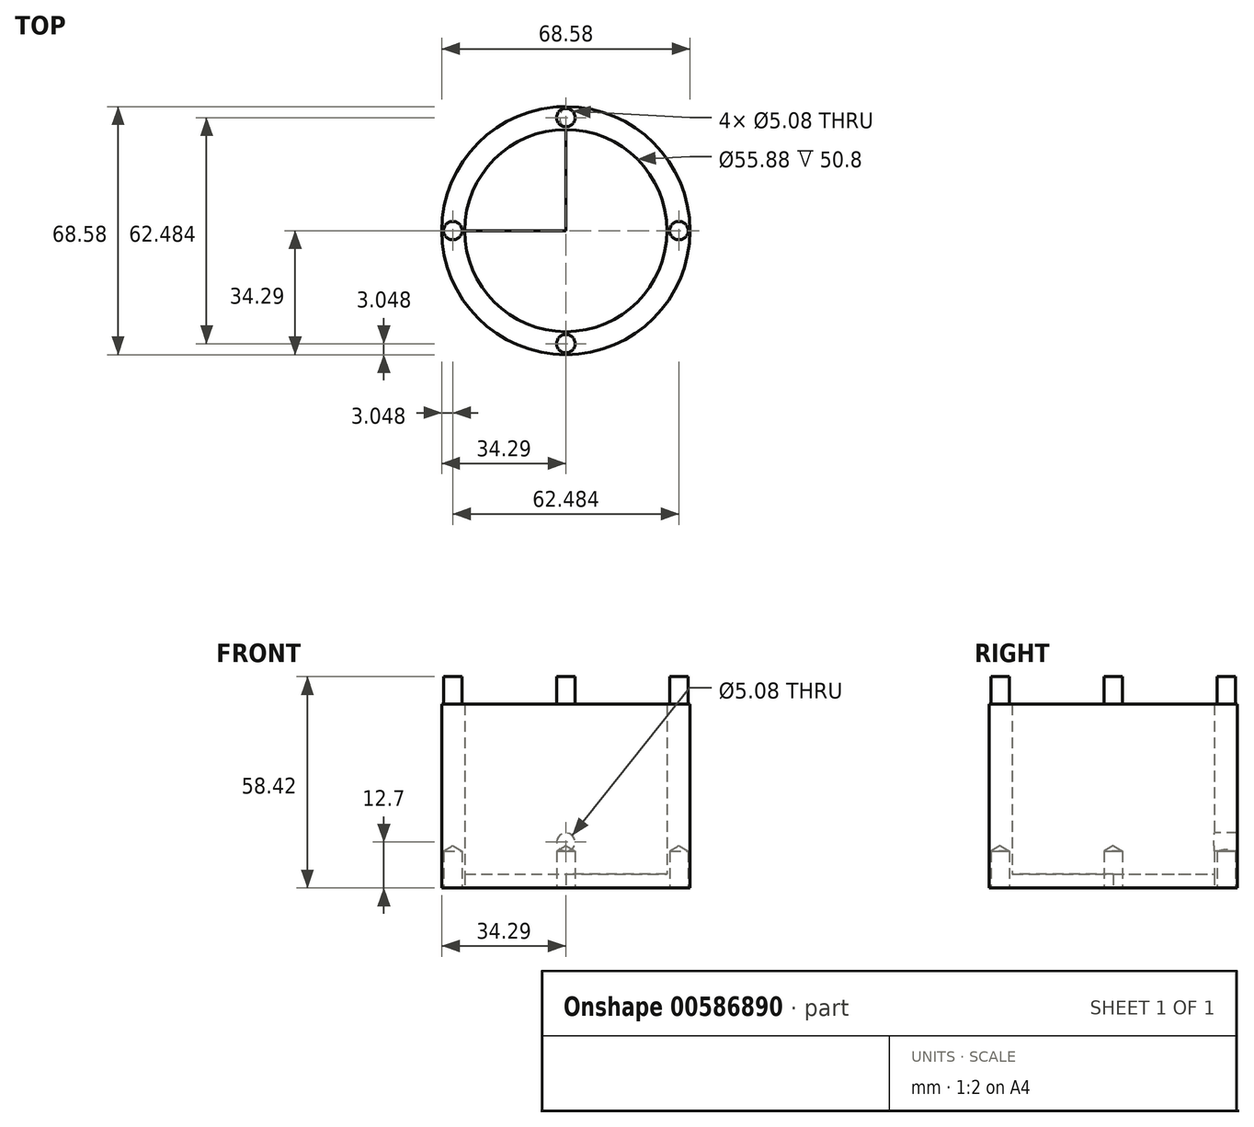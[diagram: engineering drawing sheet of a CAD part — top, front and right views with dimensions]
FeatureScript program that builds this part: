
annotation { "Feature Type Name" : "Feature", "Feature Type Description" : "" }
export const myFeature = defineFeature(function(context is Context, id is Id, definition is map)
    precondition{}
    {
        {
            var Q0;
            Q0=qCreatedBy(makeId("Front.planeOp"),FACE);
            var sketch = newSketch(context, id + "F0", { "sketchPlane" : qUnion([Q0])});
            skLineSegment(sketch, "E0.bottom", {"start": v(0, 0) * mm, "end": v(27.94, 0) * mm});
            skLineSegment(sketch, "E0.top", {"start": v(0, 20.3) * mm, "end": v(27.94, 20.3) * mm});
            skLineSegment(sketch, "E0.left", {"start": v(0, 0) * mm, "end": v(0, 20.3) * mm});
            skLineSegment(sketch, "E0.right", {"start": v(27.94, 0) * mm, "end": v(27.94, 20.3) * mm});
            skLineSegment(sketch, "E1.bottom", {"start": v(27.94, 0) * mm, "end": v(34.3, 0) * mm});
            skLineSegment(sketch, "E1.top", {"start": v(27.94, 50.8) * mm, "end": v(34.29, 50.8) * mm});
            skLineSegment(sketch, "E1.left", {"start": v(27.94, 0) * mm, "end": v(27.94, 50.8) * mm});
            skLineSegment(sketch, "E1.right", {"start": v(34.3, 0) * mm, "end": v(34.29, 50.8) * mm});
            skPoint(sketch, "E2", {"position": v(0, 12.7) * mm});
            skSolve(sketch);
        }
        {
            var Q0;
            {var subQ3=sQuery(id+"F0.wireOp",EDGE,"E1.bottom");Q0=makeQuery(id+"F0.imprint","IMPRINT",FACE,{"disambiguationData":[TD([[makeQuery(id+"F0.imprint","IMPRINT",EDGE,{"derivedFrom":subQ3}),1.0]])]});}
            var Q1;
            Q1=sQuery(id+"F0.wireOp",EDGE,"E0.left");
            revolve(context, id + "F1", {"entities" : qUnion([Q0]), "axis" : qUnion([Q1]), "revolveType" : RevolveType.FULL});
        }
        {
            var Q0;
            Q0=makeQuery(id+"F1.opRevolve","SWEPT_FACE",FACE,{"disambiguationData":[OSD([sQuery(id+"F0.wireOp",EDGE,"E1.top")])]});
            var sketch = newSketch(context, id + "F2", { "sketchPlane" : qUnion([Q0])});
            skCircle(sketch, "E3", {"center": v(0, 31.24) * mm, "radius": 2.54 * mm});
            skCircle(sketch, "E4", {"center": v(31.24, 0) * mm, "radius": 2.54 * mm});
            skCircle(sketch, "E5", {"center": v(0, -31.24) * mm, "radius": 2.54 * mm});
            skCircle(sketch, "E6", {"center": v(-31.24, 0) * mm, "radius": 2.54 * mm});
            skSolve(sketch);
        }
        {
            var Q0;
            Q0=makeQuery(id+"F2.imprint","IMPRINT",FACE,{"disambiguationData":[TD([[makeQuery(id+"F2.imprint","IMPRINT",EDGE,{"derivedFrom":sQuery(id+"F2.wireOp",EDGE,"E3")}),1.0]])]});
            var Q1;
            Q1=makeQuery(id+"F2.imprint","IMPRINT",FACE,{"disambiguationData":[TD([[makeQuery(id+"F2.imprint","IMPRINT",EDGE,{"derivedFrom":sQuery(id+"F2.wireOp",EDGE,"E4")}),1.0]])]});
            var Q2;
            Q2=makeQuery(id+"F2.imprint","IMPRINT",FACE,{"disambiguationData":[TD([[makeQuery(id+"F2.imprint","IMPRINT",EDGE,{"derivedFrom":sQuery(id+"F2.wireOp",EDGE,"E5")}),1.0]])]});
            var Q3;
            Q3=makeQuery(id+"F2.imprint","IMPRINT",FACE,{"disambiguationData":[TD([[makeQuery(id+"F2.imprint","IMPRINT",EDGE,{"derivedFrom":sQuery(id+"F2.wireOp",EDGE,"E6")}),1.0]])]});
            extrude(context, id + "F3", {"entities" : qUnion([Q0, Q1, Q2, Q3]), "operationType" : NewBodyOperationType.ADD, "depth" : 7.62 * mm, "offsetDistance" : 25.4 * mm});
        }
        {
            var Q0;
            Q0=sQuery(id+"F0.wireOp",VERTEX,"E2");
            var Q1;
            Q1=makeQuery(id+"F1.opRevolve","SWEPT_BODY",BODY,{"disambiguationData":[OSD([sQuery(id+"F0.wireOp",EDGE,"E1.bottom"),sQuery(id+"F0.wireOp",EDGE,"E1.top"),sQuery(id+"F0.wireOp",EDGE,"E1.left"),sQuery(id+"F0.wireOp",EDGE,"E1.right")])]});
            hole(context, id + "F4", {"style" : HoleStyle.SIMPLE, "endStyle" : HoleEndStyle.THROUGH, "holeDiameter" : 5.08 * mm, "majorDiameter" : 6.35 * mm, "isTappedThrough" : true, "tappedDepth" : 12.7 * mm, "tapClearance" : 3, "startFromSketch" : true, "locations" : qUnion([Q0]), "scope" : qUnion([Q1])});
        }
        {
            var Q0;
            Q0=qCreatedBy(makeId("Top.planeOp"),FACE);
            var sketch = newSketch(context, id + "F5", { "sketchPlane" : qUnion([Q0])});
            skPoint(sketch, "E7", {"position": v(0, 31.24) * mm});
            skPoint(sketch, "E8", {"position": v(-31.24, 0) * mm});
            skPoint(sketch, "E9", {"position": v(0, -31.24) * mm});
            skPoint(sketch, "E10", {"position": v(31.24, 0) * mm});
            skSolve(sketch);
        }
        {
            var Q0;
            Q0=sQuery(id+"F5.wireOp",VERTEX,"E9");
            var Q1;
            Q1=sQuery(id+"F5.wireOp",VERTEX,"E10");
            var Q2;
            Q2=sQuery(id+"F5.wireOp",VERTEX,"E7");
            var Q3;
            Q3=sQuery(id+"F5.wireOp",VERTEX,"E8");
            var Q4;
            Q4=makeQuery(id+"F1.opRevolve","SWEPT_BODY",BODY,{"disambiguationData":[OSD([sQuery(id+"F0.wireOp",EDGE,"E1.bottom"),sQuery(id+"F0.wireOp",EDGE,"E1.top"),sQuery(id+"F0.wireOp",EDGE,"E1.left"),sQuery(id+"F0.wireOp",EDGE,"E1.right")])]});
            hole(context, id + "F6", {"style" : HoleStyle.SIMPLE, "endStyle" : HoleEndStyle.BLIND, "oppositeDirection" : true, "holeDiameter" : 5.08 * mm, "majorDiameter" : 6.35 * mm, "holeDepth" : 10.16 * mm, "isTappedThrough" : true, "tappedDepth" : 12.7 * mm, "tapClearance" : 3, "startFromSketch" : true, "locations" : qUnion([Q0, Q1, Q2, Q3]), "scope" : qUnion([Q4])});
        }
        {
            var Q0;
            Q0=qCreatedBy(makeId("Top.planeOp"),FACE);
            var sketch = newSketch(context, id + "F7", { "sketchPlane" : qUnion([Q0])});
            skArc(sketch, "E11", {"start": v(-28.17, 0) * mm, "mid": v(19.92, -19.92) * mm, "end": v(0, 28.17) * mm});
            skLineSegment(sketch, "E12", {"start": v(-28.17, 0) * mm, "end": v(0, 0) * mm});
            skPoint(sketch, "E13", {"position": v(-19.12, 21.16) * mm});
            skLineSegment(sketch, "E14", {"start": v(0, 0) * mm, "end": v(0, 28.17) * mm});
            skSolve(sketch);
        }
        {
            var Q0;
            Q0=makeQuery(id+"F7.imprint","IMPRINT",FACE,{"disambiguationData":[TD([[makeQuery(id+"F7.imprint","IMPRINT",EDGE,{"derivedFrom":sQuery(id+"F7.wireOp",EDGE,"E11")}),1.0]])]});
            extrude(context, id + "F8", {"entities" : qUnion([Q0]), "operationType" : NewBodyOperationType.ADD, "depth" : 3.8 * mm, "offsetDistance" : 25.4 * mm});
        }
    });
